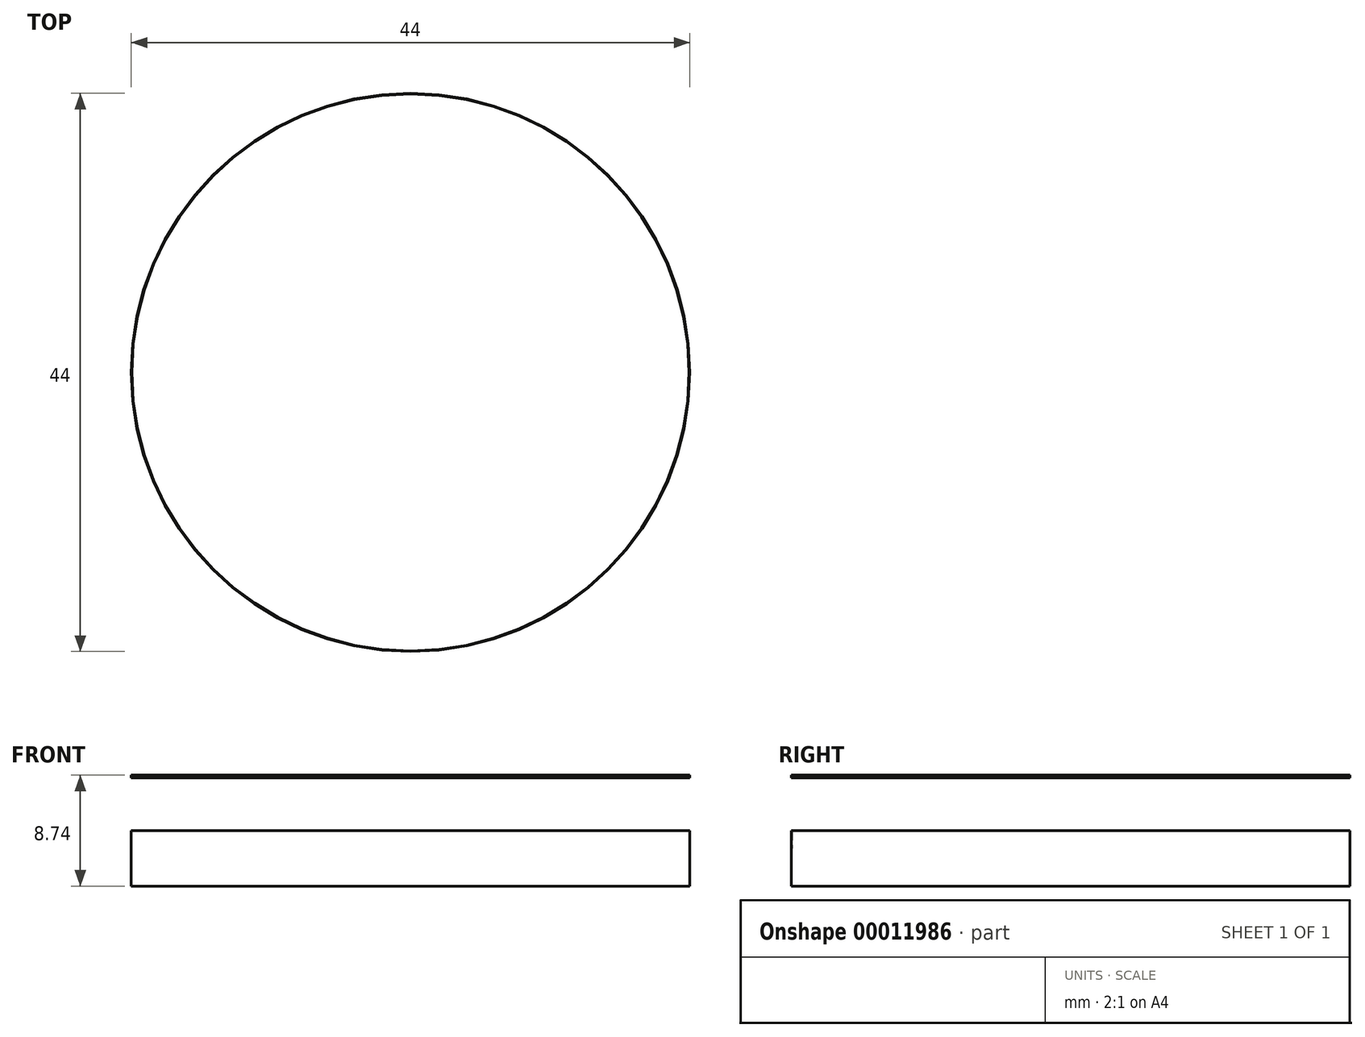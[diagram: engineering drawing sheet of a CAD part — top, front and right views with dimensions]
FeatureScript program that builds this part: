
annotation { "Feature Type Name" : "Feature", "Feature Type Description" : "" }
export const myFeature = defineFeature(function(context is Context, id is Id, definition is map)
    precondition{}
    {
        {
            var Q0;
            Q0=qCreatedBy(makeId("Front.planeOp"),FACE);
            var sketch = newSketch(context, id + "F0", { "sketchPlane" : qUnion([Q0])});
            skLineSegment(sketch, "E0", {"start": v(0, 0) * mm, "end": v(0, 74.58) * mm});
            skLineSegment(sketch, "E1", {"start": v(-22, 0) * mm, "end": v(-24, 0) * mm});
            skLineSegment(sketch, "E2.0", {"start": v(-19.95, 10) * mm, "end": v(-22, 10) * mm});
            skLineSegment(sketch, "E3.0", {"start": v(-22, 0) * mm, "end": v(-22, 10) * mm});
            skLineSegment(sketch, "E4.0", {"start": v(-24, 0) * mm, "end": v(-24, 10) * mm});
            skEllipticalArc(sketch, "E5", {});
            skArc(sketch, "E6", {"start": v(-43.8, 70) * mm, "mid": v(-46.62, 66.48) * mm, "end": v(-43.8, 62.97) * mm});
            skFitSpline(sketch, "E7.0", {"points": [v(-40.7, 72.18) * mm, v(-42, 72.28) * mm, v(-43.3, 72.18) * mm, v(-44.98, 71.8) * mm, v(-47, 70.89) * mm, v(-49.2, 69.2) * mm, v(-51.26, 67) * mm, v(-53.16, 64.29) * mm, v(-54.94, 61.1) * mm, v(-56.3, 58.04) * mm, v(-57.34, 55.37) * mm, v(-58.08, 53.25) * mm, v(-58.79, 51.03) * mm, v(-59.67, 47.95) * mm, v(-60.66, 43.9) * mm, v(-61.69, 38.76) * mm, v(-62.54, 33.36) * mm, v(-63.2, 27.75) * mm, v(-63.7, 21.96) * mm, v(-63.94, 17.02) * mm, v(-64.04, 13.02) * mm, v(-64.06, 10) * mm, v(-64.04, 6.98) * mm, v(-63.94, 2.98) * mm, v(-63.7, -1.96) * mm, v(-63.2, -7.75) * mm, v(-62.54, -13.36) * mm, v(-61.69, -18.76) * mm, v(-60.66, -23.9) * mm, v(-59.67, -27.95) * mm, v(-58.79, -31.03) * mm, v(-58.08, -33.25) * mm, v(-57.34, -35.37) * mm, v(-56.3, -38.04) * mm, v(-54.94, -41.1) * mm, v(-53.16, -44.29) * mm, v(-51.26, -47) * mm, v(-49.2, -49.2) * mm, v(-47, -50.89) * mm, v(-44.98, -51.8) * mm, v(-43.3, -52.18) * mm, v(-42, -52.28) * mm, v(-40.7, -52.18) * mm, v(-39.02, -51.8) * mm, v(-37, -50.89) * mm, v(-34.8, -49.2) * mm, v(-32.74, -47) * mm, v(-30.84, -44.29) * mm, v(-29.06, -41.1) * mm, v(-27.7, -38.04) * mm, v(-26.66, -35.37) * mm, v(-25.92, -33.25) * mm, v(-25.21, -31.03) * mm, v(-24.33, -27.95) * mm, v(-23.34, -23.9) * mm, v(-22.31, -18.76) * mm, v(-21.46, -13.36) * mm, v(-20.8, -7.75) * mm, v(-20.3, -1.96) * mm, v(-20.06, 2.98) * mm, v(-19.96, 6.98) * mm, v(-19.94, 10) * mm, v(-19.96, 13.02) * mm, v(-20.06, 17.02) * mm, v(-20.3, 21.96) * mm, v(-20.8, 27.75) * mm, v(-21.46, 33.36) * mm, v(-22.31, 38.76) * mm, v(-23.34, 43.9) * mm, v(-24.33, 47.95) * mm, v(-25.21, 51.03) * mm, v(-25.92, 53.25) * mm, v(-26.66, 55.37) * mm, v(-27.7, 58.04) * mm, v(-29.06, 61.1) * mm, v(-30.84, 64.29) * mm, v(-32.74, 67) * mm, v(-34.8, 69.2) * mm, v(-37, 70.89) * mm, v(-39.02, 71.8) * mm, v(-40.7, 72.18) * mm, v(-42, 72.28) * mm, v(-43.3, 72.18) * mm]});
            skArc(sketch, "E8.0", {"start": v(-44.24, 71.95) * mm, "mid": v(-48.62, 66.48) * mm, "end": v(-44.24, 61.02) * mm});
            skLineSegment(sketch, "E9", {"start": v(-43.8, 62.97) * mm, "end": v(-44.24, 61.02) * mm});
            skLineSegment(sketch, "E10", {"start": v(-24, 10) * mm, "end": v(-22, 14.17) * mm});
            skLineSegment(sketch, "E11.trimOffspring", {"start": v(-20.13, 18.07) * mm, "end": v(-20.13, 18.07) * mm});
            skFitSpline(sketch, "E12.trimOffspring", {"points": [v(-40.7, 72.18) * mm, v(-42, 72.28) * mm, v(-43.3, 72.18) * mm, v(-44.98, 71.8) * mm, v(-47, 70.89) * mm, v(-49.2, 69.2) * mm, v(-51.26, 67) * mm, v(-53.16, 64.29) * mm, v(-54.94, 61.1) * mm, v(-56.3, 58.04) * mm, v(-57.34, 55.37) * mm, v(-58.08, 53.25) * mm, v(-58.79, 51.03) * mm, v(-59.67, 47.95) * mm, v(-60.66, 43.9) * mm, v(-61.69, 38.76) * mm, v(-62.54, 33.36) * mm, v(-63.2, 27.75) * mm, v(-63.7, 21.96) * mm, v(-63.94, 17.02) * mm, v(-64.04, 13.02) * mm, v(-64.06, 10) * mm, v(-64.04, 6.98) * mm, v(-63.94, 2.98) * mm, v(-63.7, -1.96) * mm, v(-63.2, -7.75) * mm, v(-62.54, -13.36) * mm, v(-61.69, -18.76) * mm, v(-60.66, -23.9) * mm, v(-59.67, -27.95) * mm, v(-58.79, -31.03) * mm, v(-58.08, -33.25) * mm, v(-57.34, -35.37) * mm, v(-56.3, -38.04) * mm, v(-54.94, -41.1) * mm, v(-53.16, -44.29) * mm, v(-51.26, -47) * mm, v(-49.2, -49.2) * mm, v(-47, -50.89) * mm, v(-44.98, -51.8) * mm, v(-43.3, -52.18) * mm, v(-42, -52.28) * mm, v(-40.7, -52.18) * mm, v(-39.02, -51.8) * mm, v(-37, -50.89) * mm, v(-34.8, -49.2) * mm, v(-32.74, -47) * mm, v(-30.84, -44.29) * mm, v(-29.06, -41.1) * mm, v(-27.7, -38.04) * mm, v(-26.66, -35.37) * mm, v(-25.92, -33.25) * mm, v(-25.21, -31.03) * mm, v(-24.33, -27.95) * mm, v(-23.34, -23.9) * mm, v(-22.31, -18.76) * mm, v(-21.46, -13.36) * mm, v(-20.8, -7.75) * mm, v(-20.3, -1.96) * mm, v(-20.06, 2.98) * mm, v(-19.96, 6.98) * mm, v(-19.94, 10) * mm, v(-19.96, 13.02) * mm, v(-20.06, 17.02) * mm, v(-20.3, 21.96) * mm, v(-20.8, 27.75) * mm, v(-21.46, 33.36) * mm, v(-22.31, 38.76) * mm, v(-23.34, 43.9) * mm, v(-24.33, 47.95) * mm, v(-25.21, 51.03) * mm, v(-25.92, 53.25) * mm, v(-26.66, 55.37) * mm, v(-27.7, 58.04) * mm, v(-29.06, 61.1) * mm, v(-30.84, 64.29) * mm, v(-32.74, 67) * mm, v(-34.8, 69.2) * mm, v(-37, 70.89) * mm, v(-39.02, 71.8) * mm, v(-40.7, 72.18) * mm, v(-42, 72.28) * mm, v(-43.3, 72.18) * mm]});
            skEllipticalArc(sketch, "E13.trimOffspring", {});
            skLineSegment(sketch, "E14.trimOffspring", {"start": v(-22, 14.16) * mm, "end": v(-22, 14.37) * mm});
            skLineSegment(sketch, "E15.trimOffspring", {"start": v(-42, 10) * mm, "end": v(-87.85, 10) * mm});
            skLineSegment(sketch, "E16.trimOffspring", {"start": v(-42, 0) * mm, "end": v(-87.85, 0) * mm});
            skLineSegment(sketch, "E17.trimOffspring", {"start": v(-24, 46.56) * mm, "end": v(-24, 46.56) * mm});
            const initialGuessF0  = {"E5": [-0.042, 0.01, 0, 1, 0.06024434616905369, 0.020052911051077944, 4.639729043229353, 4.71238898038469], "E13.trimOffspring": [-0.042, 0.01, 0, 1, 0.06024434616905369, 0.020052911051077944, 4.781735492963575, 0.09009620853705362]};
            skSetInitialGuess(sketch, initialGuessF0);
            skSolve(sketch);
        }
        {
            var Q0;
            Q0 = qSketchRegion(id + "F0", true);
            var Q1;
            Q1=sQuery(id+"F0.wireOp",EDGE,"E0");
            revolve(context, id + "F1", {"entities" : qUnion([Q0]), "axis" : qUnion([Q1]), "revolveType" : RevolveType.FULL});
        }
        {
            var Q0;
            Q0=qCreatedBy(makeId("Top.planeOp"),FACE);
            var sketch = newSketch(context, id + "F2", { "sketchPlane" : qUnion([Q0])});
            skLineSegment(sketch, "E18", {"start": v(0, 0) * mm, "end": v(0, 67.07) * mm});
            skLineSegment(sketch, "E19", {"start": v(64.73, -59.73) * mm, "end": v(64.73, 67.17) * mm});
            skLineSegment(sketch, "E20", {"start": v(64.73, -59.73) * mm, "end": v(26, -59.73) * mm});
            skLineSegment(sketch, "E21.0", {"start": v(29, 67.07) * mm, "end": v(29, -59.73) * mm});
            skLineSegment(sketch, "E22", {"start": v(29, 67.07) * mm, "end": v(64.73, 67.17) * mm});
            skSolve(sketch);
        }
        {
            var Q0;
            Q0 = qSketchRegion(id + "F2", true);
            extrude(context, id + "F3", {"entities" : qUnion([Q0]), "operationType" : NewBodyOperationType.REMOVE, "endBound" : BoundingType.THROUGH_ALL, "depth" : 25 * mm});
        }
    });
